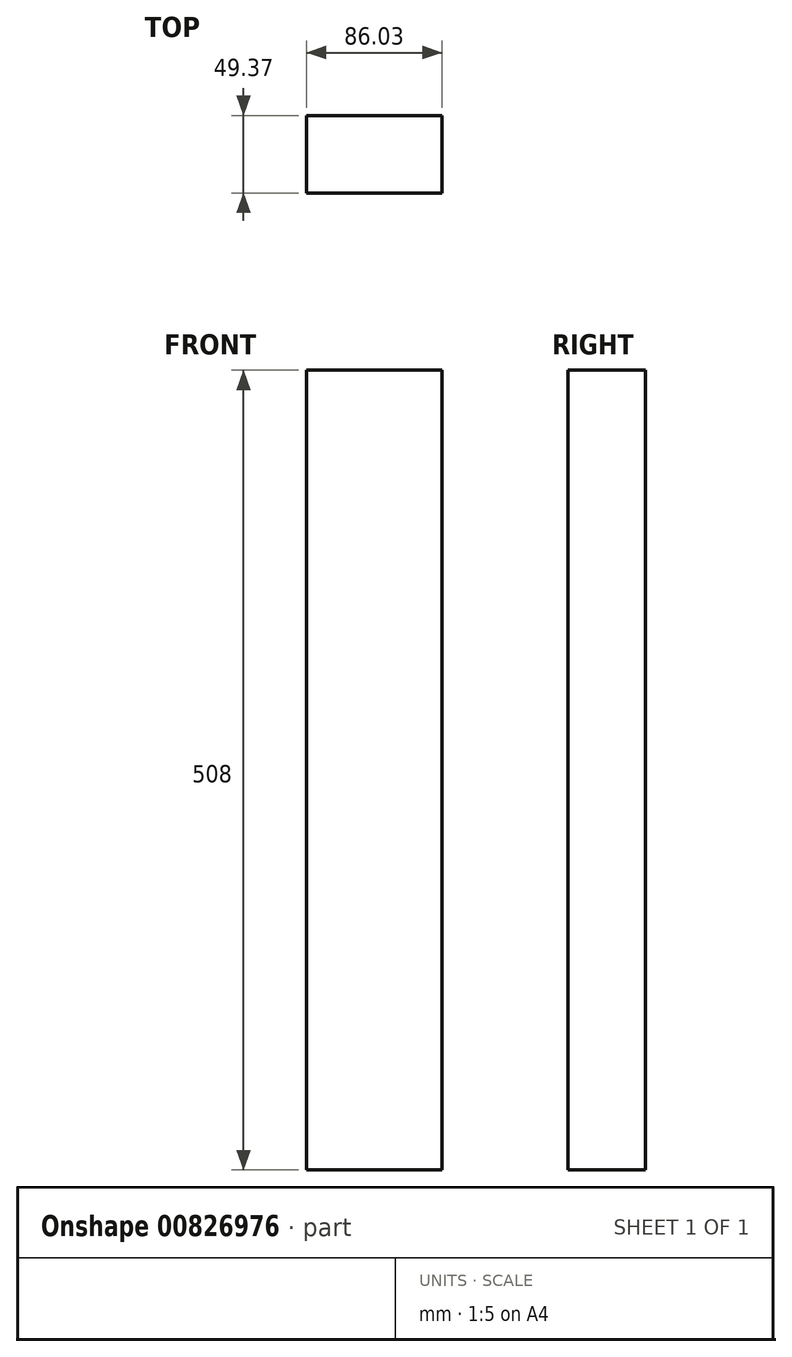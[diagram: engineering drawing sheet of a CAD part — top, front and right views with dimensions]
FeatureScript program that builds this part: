
annotation { "Feature Type Name" : "Feature", "Feature Type Description" : "" }
export const myFeature = defineFeature(function(context is Context, id is Id, definition is map)
    precondition{}
    {
        {
            var Q0;
            Q0=qCreatedBy(makeId("Top.planeOp"),FACE);
            var sketch = newSketch(context, id + "F0", { "sketchPlane" : qUnion([Q0])});
            skLineSegment(sketch, "E0", {"start": v(-40.57, 49.37) * mm, "end": v(45.46, 49.37) * mm});
            skLineSegment(sketch, "E1", {"start": v(45.46, 49.37) * mm, "end": v(45.46, 0) * mm});
            skLineSegment(sketch, "E2", {"start": v(45.46, 0) * mm, "end": v(-40.57, 0) * mm});
            skLineSegment(sketch, "E3", {"start": v(-40.57, 0) * mm, "end": v(-40.57, 49.37) * mm});
            skSolve(sketch);
        }
        {
            var Q0;
            Q0 = qSketchRegion(id + "F0", true);
            extrude(context, id + "F1", {"entities" : qUnion([Q0]), "depth" : 508 * mm, "offsetDistance" : 25.4 * mm});
        }
    });
